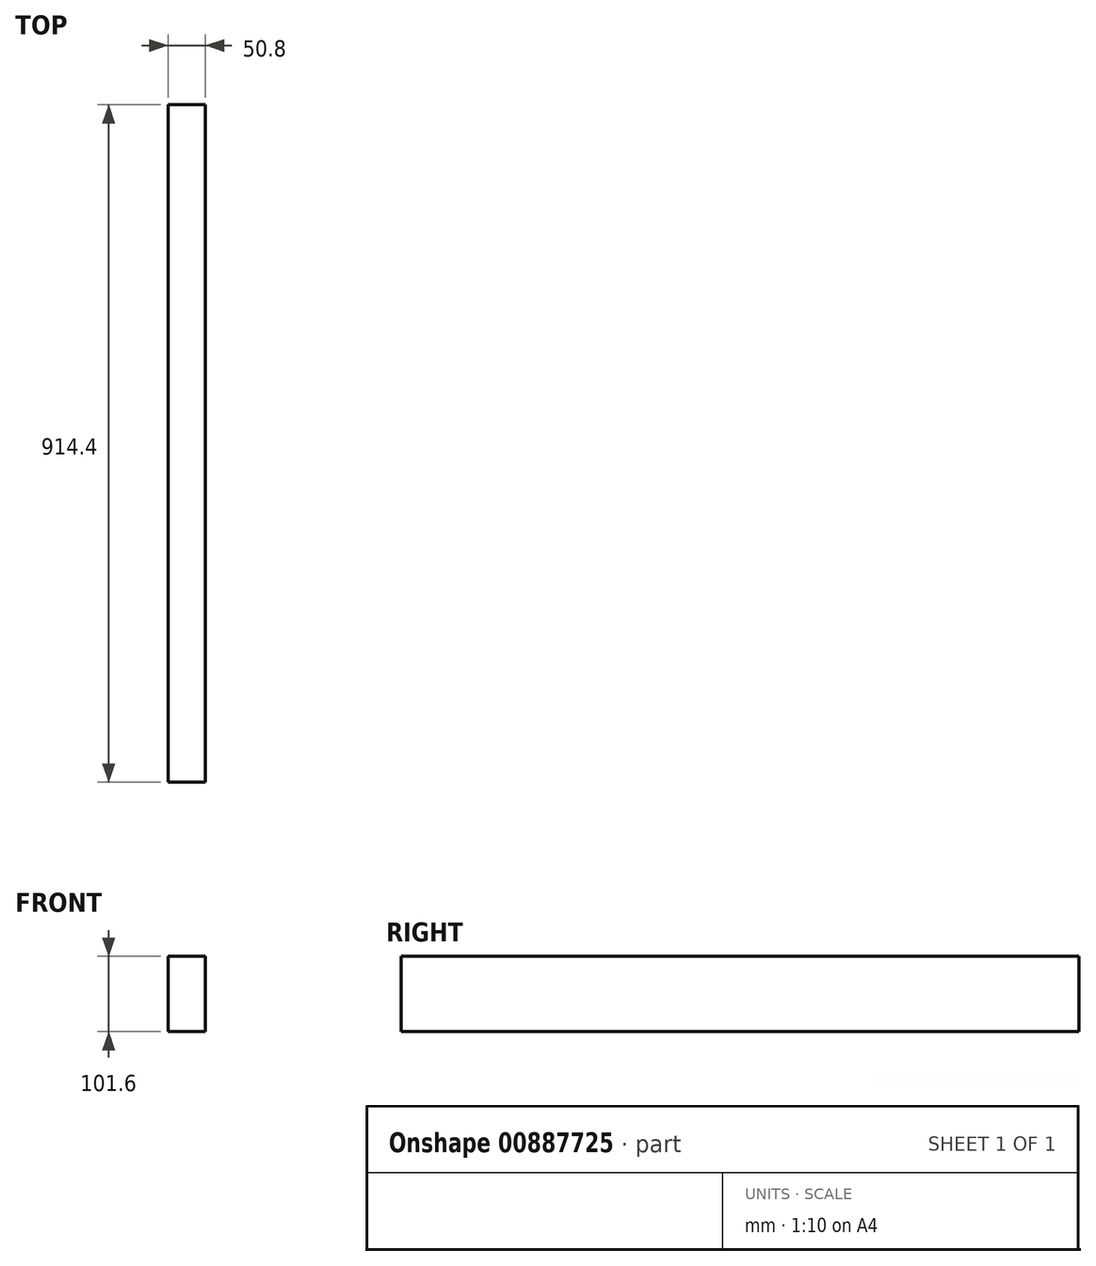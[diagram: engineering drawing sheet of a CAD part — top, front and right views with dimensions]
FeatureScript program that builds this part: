
annotation { "Feature Type Name" : "Feature", "Feature Type Description" : "" }
export const myFeature = defineFeature(function(context is Context, id is Id, definition is map)
    precondition{}
    {
        {
            var Q0;
            Q0=qCreatedBy(makeId("Front.planeOp"),FACE);
            var sketch = newSketch(context, id + "F0", { "sketchPlane" : qUnion([Q0])});
            skLineSegment(sketch, "E0.bottom", {"start": v(-50.8, 0) * mm, "end": v(0, 0) * mm});
            skLineSegment(sketch, "E0.top", {"start": v(-50.8, -101.6) * mm, "end": v(0, -101.6) * mm});
            skLineSegment(sketch, "E0.left", {"start": v(-50.8, 0) * mm, "end": v(-50.8, -101.6) * mm});
            skLineSegment(sketch, "E0.right", {"start": v(0, 0) * mm, "end": v(0, -101.6) * mm});
            skSolve(sketch);
        }
        {
            var Q0;
            Q0=makeQuery(id+"F0.imprint","IMPRINT",FACE,{"disambiguationData":[TD([[makeQuery(id+"F0.imprint","IMPRINT",EDGE,{"derivedFrom":sQuery(id+"F0.wireOp",EDGE,"E0.bottom")}),-1.0]])]});
            extrude(context, id + "F1", {"entities" : qUnion([Q0]), "depth" : 914.4 * mm, "offsetDistance" : 25.4 * mm});
        }
    });
